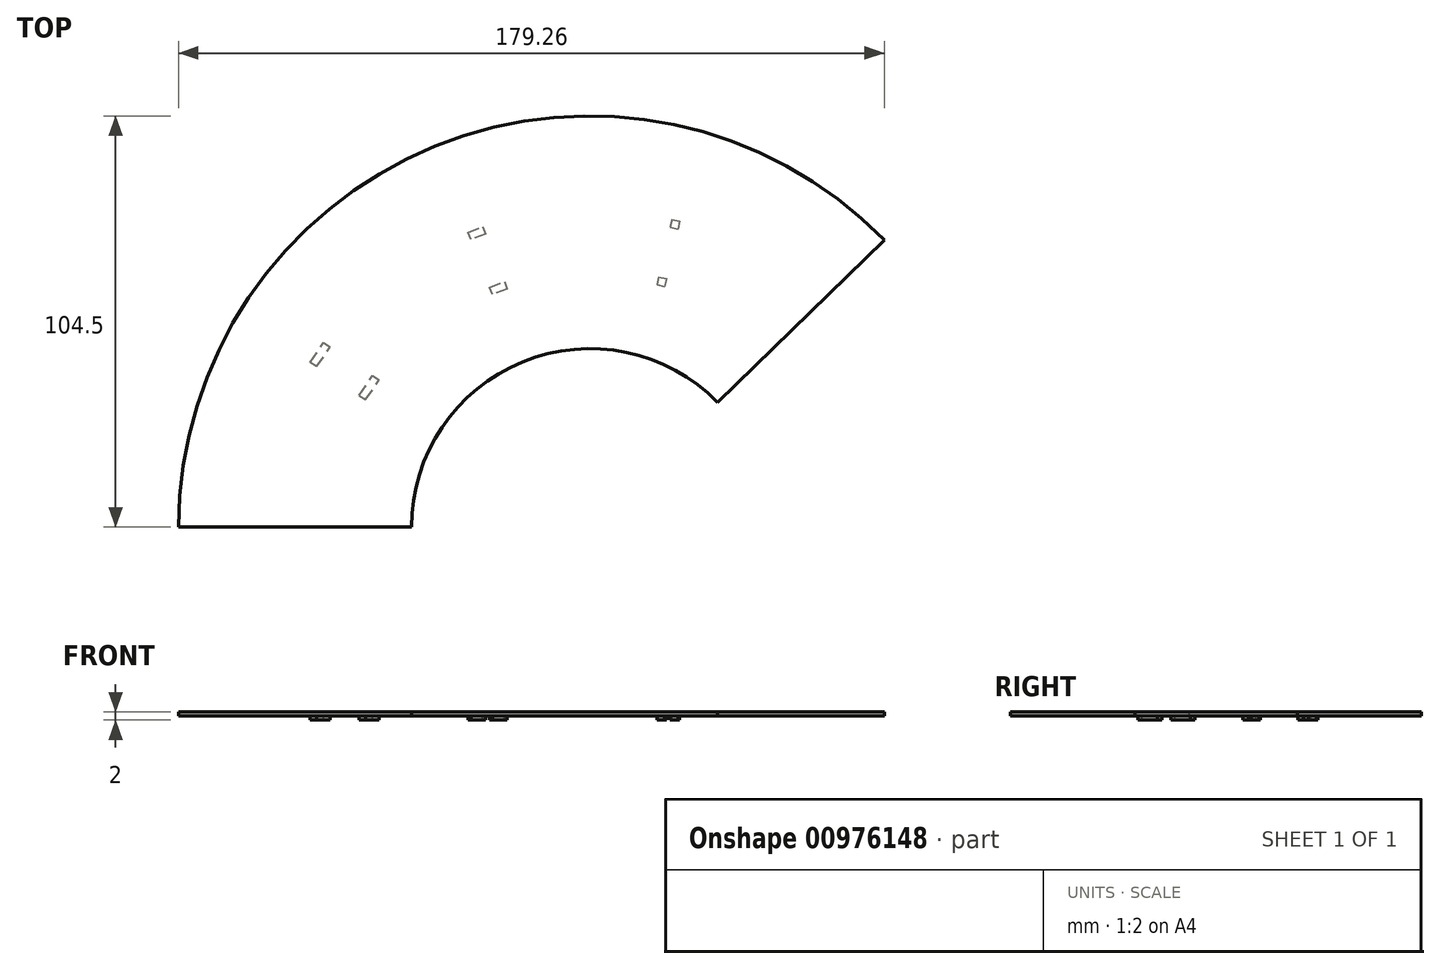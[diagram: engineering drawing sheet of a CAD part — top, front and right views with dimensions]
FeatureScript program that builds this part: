
annotation { "Feature Type Name" : "Feature", "Feature Type Description" : "" }
export const myFeature = defineFeature(function(context is Context, id is Id, definition is map)
    precondition{}
    {
        {
            var Q0;
            Q0=qCreatedBy(makeId("Top.planeOp"),FACE);
            var sketch = newSketch(context, id + "F0", { "sketchPlane" : qUnion([Q0])});
            skArc(sketch, "E0", {"start": v(74.76, 73.01) * mm, "mid": v(-39.42, 96.78) * mm, "end": v(-104.5, 0) * mm});
            skArc(sketch, "E1", {"start": v(32.44, 31.69) * mm, "mid": v(-17.1, 42) * mm, "end": v(-45.35, 0) * mm});
            skLineSegment(sketch, "E2", {"start": v(-45.35, 0) * mm, "end": v(-104.5, 0) * mm});
            skLineSegment(sketch, "E3", {"start": v(32.44, 31.69) * mm, "end": v(74.76, 73.01) * mm});
            skSolve(sketch);
        }
        {
            var Q0;
            Q0 = qSketchRegion(id + "F0", true);
            extrude(context, id + "F1", {"entities" : qUnion([Q0]), "depth" : 1 * mm, "offsetDistance" : 25 * mm});
        }
        {
            var Q0;
            Q0=makeQuery(id+"F1.opExtrude","CAP_FACE",FACE,{"disambiguationData":[OSD([sQuery(id+"F0.wireOp",EDGE,"E0"),sQuery(id+"F0.wireOp",EDGE,"E1"),sQuery(id+"F0.wireOp",EDGE,"E2"),sQuery(id+"F0.wireOp",EDGE,"E3")])],"isStart":false});
            var sketch = newSketch(context, id + "F2", { "sketchPlane" : qUnion([Q0])});
            skLineSegment(sketch, "E4", {"start": v(-17.1, 42) * mm, "end": v(-39.42, 96.78) * mm});
            skLineSegment(sketch, "E5", {"start": v(-38.13, 24.55) * mm, "end": v(-87.2, 57.58) * mm});
            skLineSegment(sketch, "E6", {"start": v(10.49, 44.12) * mm, "end": v(22.52, 102.04) * mm});
            skLineSegment(sketch, "E7", {"start": v(-54.72, 35.71) * mm, "end": v(-55.84, 34.05) * mm});
            skLineSegment(sketch, "E8", {"start": v(-55.84, 34.05) * mm, "end": v(-57.5, 35.17) * mm});
            skLineSegment(sketch, "E9", {"start": v(-57.5, 35.17) * mm, "end": v(-56.38, 36.83) * mm});
            skLineSegment(sketch, "E10", {"start": v(-56.38, 36.83) * mm, "end": v(-55.27, 38.49) * mm});
            skLineSegment(sketch, "E11", {"start": v(-55.27, 38.49) * mm, "end": v(-53.6, 37.37) * mm});
            skLineSegment(sketch, "E12", {"start": v(-54.72, 35.71) * mm, "end": v(-53.6, 37.37) * mm});
            skLineSegment(sketch, "E13", {"start": v(-67.17, 44.09) * mm, "end": v(-68.29, 42.43) * mm});
            skLineSegment(sketch, "E14", {"start": v(-68.29, 42.43) * mm, "end": v(-69.94, 43.55) * mm});
            skLineSegment(sketch, "E15", {"start": v(-69.94, 43.55) * mm, "end": v(-68.83, 45.2) * mm});
            skLineSegment(sketch, "E16", {"start": v(-68.83, 45.2) * mm, "end": v(-67.71, 46.86) * mm});
            skLineSegment(sketch, "E17", {"start": v(-67.71, 46.86) * mm, "end": v(-66.05, 45.75) * mm});
            skLineSegment(sketch, "E18", {"start": v(-67.17, 44.09) * mm, "end": v(-66.05, 45.75) * mm});
            skLineSegment(sketch, "E19.1.0", {"start": v(-30.98, 74.88) * mm, "end": v(-29.12, 75.62) * mm});
            skLineSegment(sketch, "E19.1.1", {"start": v(-29.12, 75.62) * mm, "end": v(-27.26, 76.35) * mm});
            skLineSegment(sketch, "E19.1.2", {"start": v(-28.39, 73.76) * mm, "end": v(-26.53, 74.5) * mm});
            skLineSegment(sketch, "E19.1.3", {"start": v(-27.26, 76.35) * mm, "end": v(-26.53, 74.5) * mm});
            skLineSegment(sketch, "E19.1.4", {"start": v(-28.39, 73.76) * mm, "end": v(-30.25, 73.02) * mm});
            skLineSegment(sketch, "E19.1.5", {"start": v(-30.25, 73.02) * mm, "end": v(-30.98, 74.88) * mm});
            skLineSegment(sketch, "E19.1.6", {"start": v(-25.47, 60.93) * mm, "end": v(-23.6, 61.67) * mm});
            skLineSegment(sketch, "E19.1.7", {"start": v(-23.6, 61.67) * mm, "end": v(-21.75, 62.4) * mm});
            skLineSegment(sketch, "E19.1.8", {"start": v(-21.75, 62.4) * mm, "end": v(-21.01, 60.54) * mm});
            skLineSegment(sketch, "E19.1.9", {"start": v(-22.87, 59.8) * mm, "end": v(-21.01, 60.54) * mm});
            skLineSegment(sketch, "E19.1.10", {"start": v(-22.87, 59.8) * mm, "end": v(-24.73, 59.07) * mm});
            skLineSegment(sketch, "E19.1.11", {"start": v(-24.73, 59.07) * mm, "end": v(-25.47, 60.93) * mm});
            skLineSegment(sketch, "E19.2.1", {"start": v(20.83, 78.2) * mm, "end": v(22.78, 77.75) * mm});
            skLineSegment(sketch, "E19.2.2", {"start": v(20.38, 76.25) * mm, "end": v(22.33, 75.8) * mm});
            skLineSegment(sketch, "E19.2.3", {"start": v(22.78, 77.75) * mm, "end": v(22.33, 75.8) * mm});
            skLineSegment(sketch, "E19.2.7", {"start": v(17.47, 63.58) * mm, "end": v(19.42, 63.13) * mm});
            skLineSegment(sketch, "E19.2.8", {"start": v(19.42, 63.13) * mm, "end": v(18.97, 61.18) * mm});
            skLineSegment(sketch, "E19.2.9", {"start": v(17.02, 61.63) * mm, "end": v(18.97, 61.18) * mm});
            skPoint(sketch, "E19.center", {"position": v(0, -3.52) * mm});
            skLineSegment(sketch, "E19.anchor1", {"start": v(0, -3.52) * mm, "end": v(-69.94, 43.55) * mm, "construction": true});
            skLineSegment(sketch, "E19.anchor2", {"start": v(0, -3.52) * mm, "end": v(18.51, 77.06) * mm, "construction": true});
            skLineSegment(sketch, "E20", {"start": v(17.47, 63.58) * mm, "end": v(17.02, 61.63) * mm});
            skLineSegment(sketch, "E21", {"start": v(20.83, 78.2) * mm, "end": v(20.38, 76.25) * mm});
            skLineSegment(sketch, "E22", {"start": v(-68.29, 42.43) * mm, "end": v(-69.4, 40.77) * mm});
            skLineSegment(sketch, "E23", {"start": v(-69.4, 40.77) * mm, "end": v(-71.06, 41.89) * mm});
            skLineSegment(sketch, "E24", {"start": v(-71.06, 41.89) * mm, "end": v(-69.94, 43.55) * mm});
            skLineSegment(sketch, "E25", {"start": v(-57.5, 35.17) * mm, "end": v(-58.62, 33.51) * mm});
            skLineSegment(sketch, "E26", {"start": v(-58.62, 33.51) * mm, "end": v(-56.96, 32.4) * mm});
            skLineSegment(sketch, "E27", {"start": v(-56.96, 32.4) * mm, "end": v(-55.84, 34.05) * mm});
            skSolve(sketch);
        }
        {
            var Q0;
            Q0 = qSketchRegion(id + "F2", true);
            extrude(context, id + "F3", {"entities" : qUnion([Q0]), "operationType" : NewBodyOperationType.ADD, "oppositeDirection" : true, "depth" : 2 * mm, "offsetDistance" : 25 * mm});
        }
    });
